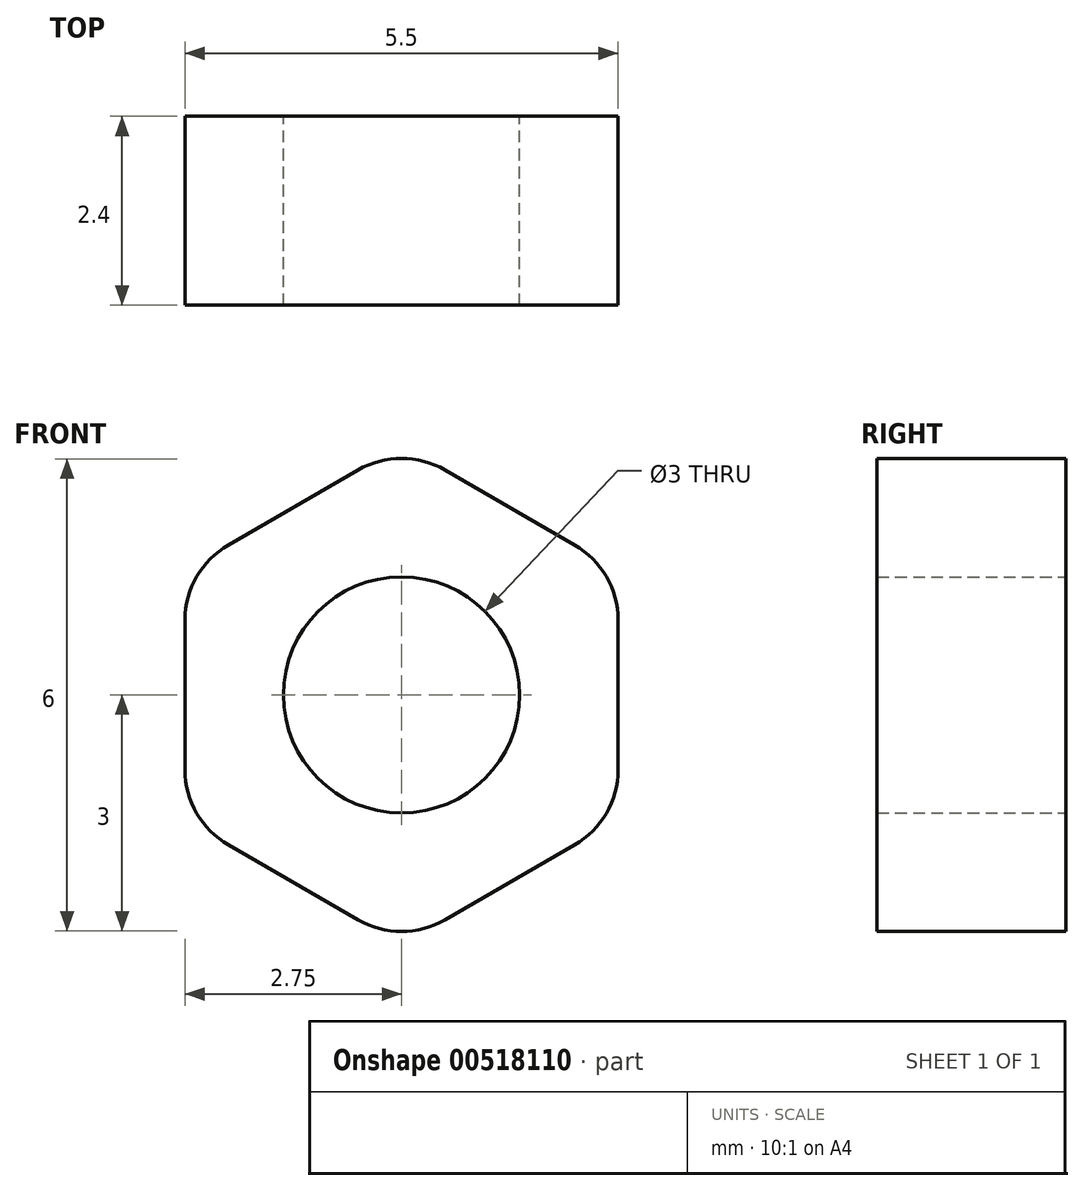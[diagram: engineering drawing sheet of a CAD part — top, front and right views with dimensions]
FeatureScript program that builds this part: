
annotation { "Feature Type Name" : "Feature", "Feature Type Description" : "" }
export const myFeature = defineFeature(function(context is Context, id is Id, definition is map)
    precondition{}
    {
        {
            assignVariable(context, id + "F0", {"name" : "m", "anyValue" : 2.4});
        }
        {
            var Q0;
            Q0=qCreatedBy(makeId("Front.planeOp"),FACE);
            var sketch = newSketch(context, id + "F1", { "sketchPlane" : qUnion([Q0])});
            skLineSegment(sketch, "E0", {"start": v(-0.55, 2.86) * mm, "end": v(-2.2, 1.9) * mm});
            skLineSegment(sketch, "E1", {"start": v(-2.75, 0.95) * mm, "end": v(-2.75, -0.95) * mm});
            skLineSegment(sketch, "E2", {"start": v(-2.2, -1.9) * mm, "end": v(-0.55, -2.86) * mm});
            skLineSegment(sketch, "E3", {"start": v(0.55, -2.86) * mm, "end": v(2.2, -1.9) * mm});
            skLineSegment(sketch, "E4", {"start": v(2.75, -0.95) * mm, "end": v(2.75, 0.95) * mm});
            skLineSegment(sketch, "E5", {"start": v(2.2, 1.9) * mm, "end": v(0.55, 2.86) * mm});
            skCircle(sketch, "E6", {"center": v(0, 0) * mm, "radius": 1.5 * mm});
            skLineSegment(sketch, "E7", {"start": v(0, 3.18) * mm, "end": v(0, -3.18) * mm, "construction": true});
            skLineSegment(sketch, "E8", {"start": v(-2.75, 0) * mm, "end": v(2.75, 0) * mm, "construction": true});
            skPoint(sketch, "E9.visualSharp", {"position": v(0, 3.18) * mm});
            skArc(sketch, "E9.filletArc", {"start": v(0.55, 2.86) * mm, "mid": v(0, 3) * mm, "end": v(-0.55, 2.86) * mm});
            skPoint(sketch, "E10.visualSharp", {"position": v(2.75, 1.59) * mm});
            skArc(sketch, "E10.filletArc", {"start": v(2.75, 0.95) * mm, "mid": v(2.6, 1.5) * mm, "end": v(2.2, 1.9) * mm});
            skPoint(sketch, "E11.visualSharp", {"position": v(2.75, -1.59) * mm});
            skArc(sketch, "E11.filletArc", {"start": v(2.2, -1.9) * mm, "mid": v(2.6, -1.5) * mm, "end": v(2.75, -0.95) * mm});
            skPoint(sketch, "E12.visualSharp", {"position": v(0, -3.18) * mm});
            skArc(sketch, "E12.filletArc", {"start": v(-0.55, -2.86) * mm, "mid": v(0, -3) * mm, "end": v(0.55, -2.86) * mm});
            skPoint(sketch, "E13.visualSharp", {"position": v(-2.75, -1.59) * mm});
            skArc(sketch, "E13.filletArc", {"start": v(-2.75, -0.95) * mm, "mid": v(-2.6, -1.5) * mm, "end": v(-2.2, -1.9) * mm});
            skPoint(sketch, "E14.visualSharp", {"position": v(-2.75, 1.59) * mm});
            skArc(sketch, "E14.filletArc", {"start": v(-2.2, 1.9) * mm, "mid": v(-2.6, 1.5) * mm, "end": v(-2.75, 0.95) * mm});
            skLineSegment(sketch, "E15", {"start": v(1.38, 2.38) * mm, "end": v(-1.37, -2.38) * mm, "construction": true});
            skSolve(sketch);
        }
        {
            var Q0;
            Q0=makeQuery(id+"F1.imprint","IMPRINT",FACE,{"disambiguationData":[TD([[makeQuery(id+"F1.imprint","IMPRINT",EDGE,{"derivedFrom":sQuery(id+"F1.wireOp",EDGE,"E0")}),1.0]])]});
            extrude(context, id + "F2", {"entities" : qUnion([Q0]), "depth" : (getVariable(context, 'm')) * mm, "offsetDistance" : 25 * mm});
        }
    });
